# Revit family: Plumbing-Faucet-Sloan-Valve-SF-2350
name_source: partatom
category: Plumbing Fixtures
units: mm (PartAtom-declared; Revit-internal decimal feet)

## family parameters
Cut with Voids When Loaded = No
Host = Face
OmniClass Number = 23.45.55.14
OmniClass Title = Single Faucets
Part Type = Normal
Room Calculation Point = No
Round Connector Dimension = Use Diameter
Shared = No

## types (5) — shared parameters
Assembly Code = D2010
CW Connection = Yes
CWFU = 1.5
Cold Water Connection Diameter = 0"
Default Elevation = 0"
Depth = 6"
Edition number = 1
HW Connection = Yes
HWFU = 1.5
Height = 4 3/4"
Hot Water Connection Diameter = 0"
Keynote = 15410
Manufacturer = Sloan Valve
Product Material = Sloan Valve - Finish - Polished Chrome
Product data url = https://bimobject.com
URL = www.sloanvalve.com
Valve Pressure Drop = 0.00 psi
Vent Connection = No
Waste Connection = No
Width = 6 1/4"
zero-valued in all types: WFU

## per-type parameters (varying)
| type | Description | Part Number | Water Flow |
| SF-2350-BAT-BDM-CP-0.35GPM-MLM-IR-FCT | Battery Power Supply, Below Deck Manual Mixing Valve, Polished Chrome Finish, 0.35 gpm, Multi-Laminar Spray, Infrared Sensor, Sloan® Battery-Powered Deck-Mounted Mid Integrated Base Body Faucet. | 3362174 | 0 GPM |
| SF-2350-BAT-BDM-CP-0.5GPM-MLM-IR-FCT | Battery Power Supply, Below Deck Manual Mixing Valve, Polished Chrome Finish, 0.5 gpm, Multi-Laminar Spray, Infrared Sensor, Sloan® Battery-Powered Deck-Mounted Mid Integrated Base Body Faucet. | 3362118 | 1 GPM |
| SF-2350-BAT-BDT-CP-0.5GPM-MLM-IR-FCT | Battery Power Supply, Below Deck Thermostatic Mixing Valve, Polished Chrome Finish, 0.5 gpm, Multi-Laminar Spray, Infrared Sensor, Sloan® Battery-Powered Deck-Mounted Mid Integrated Base Body Faucet. | 3362154 | 1 GPM |
| SF-2350-BAT-TEE-CP-0.35GPM-MLM-IR-FCT | Battery Power Supply, Below Deck Thermostatic Mixing Valve, Polished Chrome Finish, 0.5 gpm, Multi-Laminar Spray, Infrared Sensor, Sloan® Battery-Powered Deck-Mounted Mid Integrated Base Body Faucet. | 3362171 | 0 GPM |
| SF-2350-BAT-TEE-CP-0.5GPM-MLM-IR-FCT | Battery Power Supply, Back-Check Tee, Polished Chrome Finish, 0.5 gpm, Multi-Laminar Spray, Infrared Sensor, Sloan® Battery-Powered Deck-Mounted Mid Integrated Base Body Faucet. | 3362119 | 1 GPM |

note: column(s) folded — value = type name in every type: Model

## geometry (parser evidence)
native form markers: Sweep x6
no freeform markers — native parametric forms only
